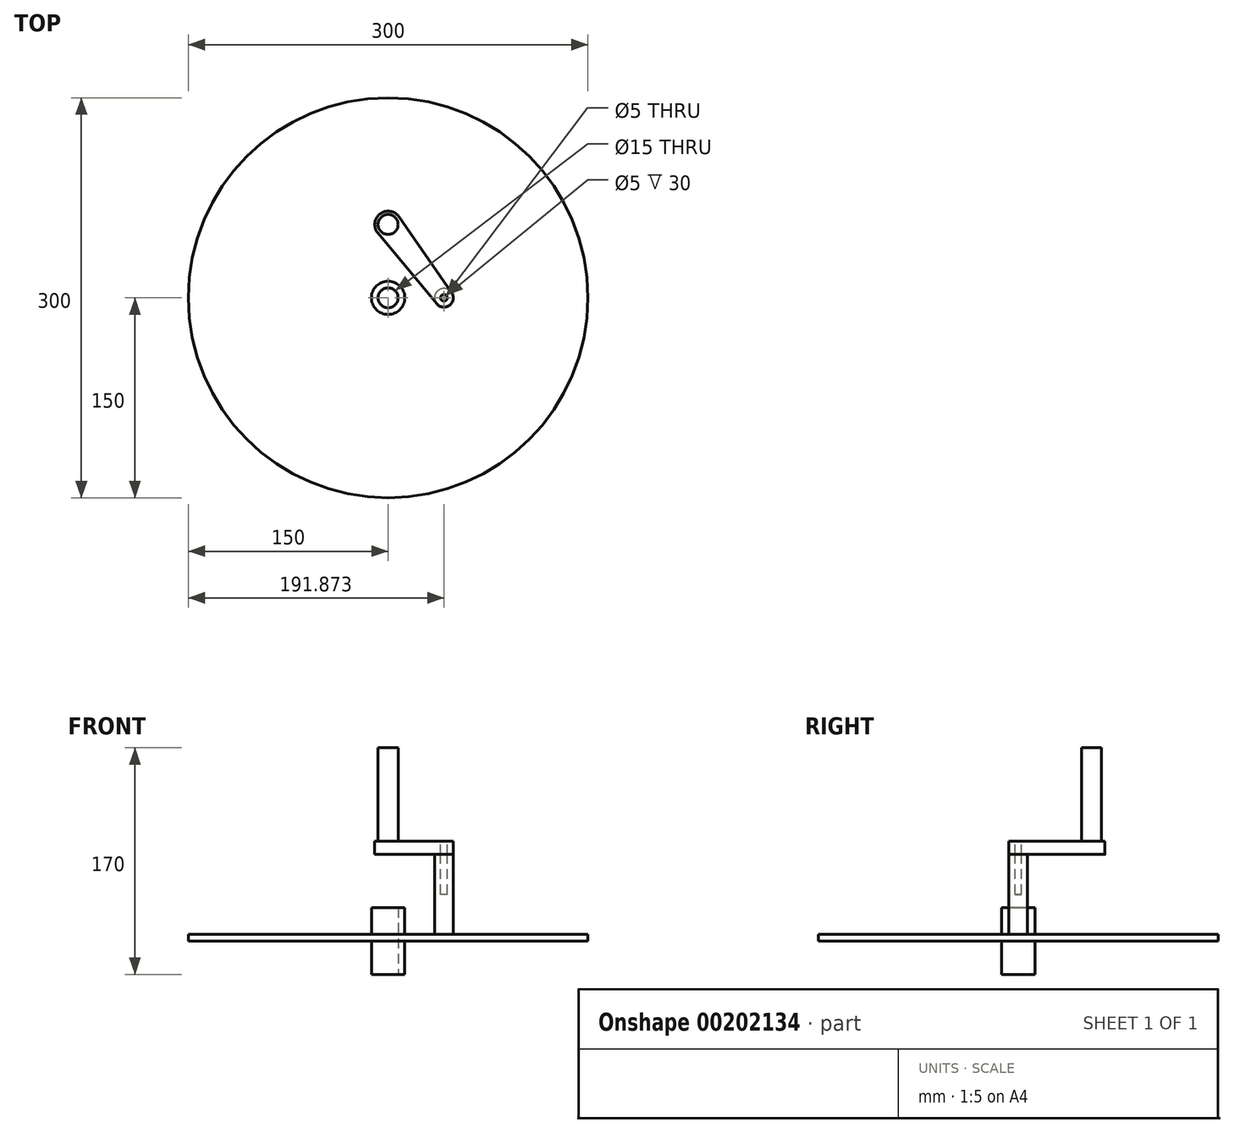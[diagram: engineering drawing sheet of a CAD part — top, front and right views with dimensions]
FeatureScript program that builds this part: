
annotation { "Feature Type Name" : "Feature", "Feature Type Description" : "" }
export const myFeature = defineFeature(function(context is Context, id is Id, definition is map)
    precondition{}
    {
        {
            var Q0;
            Q0=qCreatedBy(makeId("Top.planeOp"),FACE);
            var sketch = newSketch(context, id + "F0", { "sketchPlane" : qUnion([Q0])});
            skCircle(sketch, "E0", {"center": v(0, 0) * mm, "radius": 150 * mm});
            skSolve(sketch);
        }
        {
            var Q0;
            Q0 = qSketchRegion(id + "F0", true);
            extrude(context, id + "F1", {"entities" : qUnion([Q0]), "depth" : 5 * mm});
        }
        {
            var Q0;
            Q0=qCreatedBy(makeId("Top.planeOp"),FACE);
            var sketch = newSketch(context, id + "F2", { "sketchPlane" : qUnion([Q0])});
            skCircle(sketch, "E1", {"center": v(0, 0) * mm, "radius": 7.5 * mm});
            skCircle(sketch, "E2", {"center": v(0, 0) * mm, "radius": 12.5 * mm});
            skSolve(sketch);
        }
        {
            var Q0;
            Q0=makeQuery(id+"F2.imprint","IMPRINT",FACE,{"disambiguationData":[TD([[makeQuery(id+"F2.imprint","IMPRINT",EDGE,{"derivedFrom":sQuery(id+"F2.wireOp",EDGE,"E1")}),1.0]])]});
            extrude(context, id + "F3", {"entities" : qUnion([Q0]), "operationType" : NewBodyOperationType.REMOVE, "endBound" : BoundingType.THROUGH_ALL, "depth" : 25 * mm});
        }
        {
            var Q0;
            Q0 = qSketchRegion(id + "F2", true);
            extrude(context, id + "F4", {"entities" : qUnion([Q0]), "operationType" : NewBodyOperationType.ADD, "depth" : 25 * mm});
        }
        {
            var Q0;
            Q0 = qSketchRegion(id + "F2", true);
            extrude(context, id + "F5", {"entities" : qUnion([Q0]), "operationType" : NewBodyOperationType.ADD, "oppositeDirection" : true, "depth" : 25 * mm});
        }
        {
            var Q0;
            Q0=makeQuery(id+"F1.opExtrude","CAP_FACE",FACE,{"disambiguationData":[OSD([sQuery(id+"F0.wireOp",EDGE,"E0")])],"isStart":false});
            var sketch = newSketch(context, id + "F6", { "sketchPlane" : qUnion([Q0])});
            skCircle(sketch, "E3", {"center": v(41.87, 0) * mm, "radius": 7 * mm});
            skSolve(sketch);
        }
        {
            var Q0;
            Q0 = qSketchRegion(id + "F6", true);
            extrude(context, id + "F7", {"entities" : qUnion([Q0]), "operationType" : NewBodyOperationType.ADD, "depth" : 60 * mm});
        }
        {
            var Q0;
            Q0=makeQuery(id+"F7.opExtrude","CAP_FACE",FACE,{"disambiguationData":[OSD([sQuery(id+"F6.wireOp",EDGE,"E3")])],"isStart":false});
            var sketch = newSketch(context, id + "F8", { "sketchPlane" : qUnion([Q0])});
            skCircle(sketch, "E4", {"center": v(0, 55) * mm, "radius": 10 * mm});
            skLineSegment(sketch, "E5", {"start": v(8.21, 60.7) * mm, "end": v(47.62, 4) * mm});
            skLineSegment(sketch, "E6", {"start": v(-7.69, 48.6) * mm, "end": v(36.5, -4.48) * mm});
            skSolve(sketch);
        }
        {
            var Q0;
            Q0 = qSketchRegion(id + "F8", true);
            var Q1;
            {var subQ0=sQuery(id+"F8.wireOp",EDGE,"E5");Q1=makeQuery(id+"F8.imprint","IMPRINT",FACE,{"disambiguationData":[TD([[makeQuery(id+"F8.imprint","IMPRINT",EDGE,{"derivedFrom":subQ0}),-1.0]])]});}
            var Q2;
            {var subQ0=makeQuery(id+"F7.opExtrude","CAP_EDGE",EDGE,{"disambiguationData":[OSD([sQuery(id+"F6.wireOp",EDGE,"E3")])],"isStart":false});var subQ1=makeQuery(id+"F8.imprint","INTERSECT",VERTEX,{"derivedFrom":[subQ0,sQuery(id+"F8.wireOp",EDGE,"E5")]});Q2=makeQuery(id+"F8.imprint","IMPRINT",FACE,{"disambiguationData":[TD([[makeQuery(id+"F8.imprint","IMPRINT",EDGE,{"disambiguationData":[TD([[subQ1,1.0]])],"derivedFrom":subQ0}),1.0]])]});}
            extrude(context, id + "F9", {"entities" : qUnion([Q0, Q1, Q2]), "depth" : 10 * mm});
        }
        {
            var Q0;
            Q0=makeQuery(id+"F9.opExtrude","CAP_FACE",FACE,{"disambiguationData":[OSD([sQuery(id+"F6.wireOp",EDGE,"E3"),sQuery(id+"F8.wireOp",EDGE,"E4"),sQuery(id+"F8.wireOp",EDGE,"E5"),sQuery(id+"F8.wireOp",EDGE,"E6")])],"isStart":false});
            var sketch = newSketch(context, id + "F10", { "sketchPlane" : qUnion([Q0])});
            skCircle(sketch, "E7", {"center": v(0, 55) * mm, "radius": 7.5 * mm});
            skSolve(sketch);
        }
        {
            var Q0;
            Q0 = qSketchRegion(id + "F10", true);
            extrude(context, id + "F11", {"entities" : qUnion([Q0]), "operationType" : NewBodyOperationType.ADD, "depth" : 70 * mm});
        }
        {
            var Q0;
            Q0=makeQuery(id+"F9.opExtrude","CAP_FACE",FACE,{"disambiguationData":[OSD([sQuery(id+"F6.wireOp",EDGE,"E3"),sQuery(id+"F8.wireOp",EDGE,"E4"),sQuery(id+"F8.wireOp",EDGE,"E5"),sQuery(id+"F8.wireOp",EDGE,"E6")])],"isStart":false});
            var sketch = newSketch(context, id + "F12", { "sketchPlane" : qUnion([Q0])});
            skCircle(sketch, "E8", {"center": v(41.87, 0) * mm, "radius": 2.5 * mm});
            skSolve(sketch);
        }
        {
            var Q0;
            Q0=makeQuery(id+"F12.imprint","IMPRINT",FACE,{"disambiguationData":[TD([[makeQuery(id+"F12.imprint","IMPRINT",EDGE,{"derivedFrom":sQuery(id+"F12.wireOp",EDGE,"E8")}),1.0]])]});
            extrude(context, id + "F13", {"entities" : qUnion([Q0]), "operationType" : NewBodyOperationType.REMOVE, "oppositeDirection" : true, "depth" : 40 * mm});
        }
    });
